# Revit family: HVAC_Flue-Fan_DaVinci_InLine-LowPower-Vent
name_source: partatom
category: Mechanical Equipment
units: mm (PartAtom-declared; Revit-internal decimal feet)

## family parameters
Always vertical = No
Classification Number = 23.75.35.17.11
Cut with Voids When Loaded = No
Maintain Annotation Orientation = No
Part Type = Normal
Room Calculation Point = No
Round Connector Dimension = Use Diameter
Shared = No
Work Plane-Based = Yes

## types (1)
- as Specified
    Assembly Code = D3060500
    Construction Details = http://www.arcat.com
    Default Elevation = 0' - 0"
    Description = DaVinci In Line Interior Power Vent - RSIF 160 as Specified
    Electrical_Amperage = 3 A
    Electrical_Number of Poles = 1
    Electrical_Phase = 1
    Electrical_Voltage = 120 V
    Electrical_Wattage = 160 W
    Expected Lifespan (Years) = 0
    Keynote = 10 31 00
    Maintenance Schedule (Months) = 0
    Manufacturer = DaVinci Custom Fireplaces
    Manufacturer Fax = 425-609-2781
    Manufacturer Website = http://www.davincifireplace.com
    Model = RSIF 160
    Motor HP = 0.2
    Motor RPM = 1600
    Operating Temperature = 400 °F
    Product Data = http://www.arcat.com
    Revision = R1_2017-08
    Sales Information = http://www.davincifireplace.com
    SpecWizard = http://www.arcat.com
    Specification = http://www.arcat.com
    Type Comments = Avoid Installing Motor Face Down
    URL = http://www.davincifireplace.com
    Unit Depth = 1' - 2 1/4"
    Unit Height = 1' - 0 5/8"
    Unit Weight = 38
    Unit Width = 1' - 5 3/8"
    Warranty Duration (Years) = 0

## geometry (parser evidence)
native form markers: Sweep x5
no freeform markers — native parametric forms only
